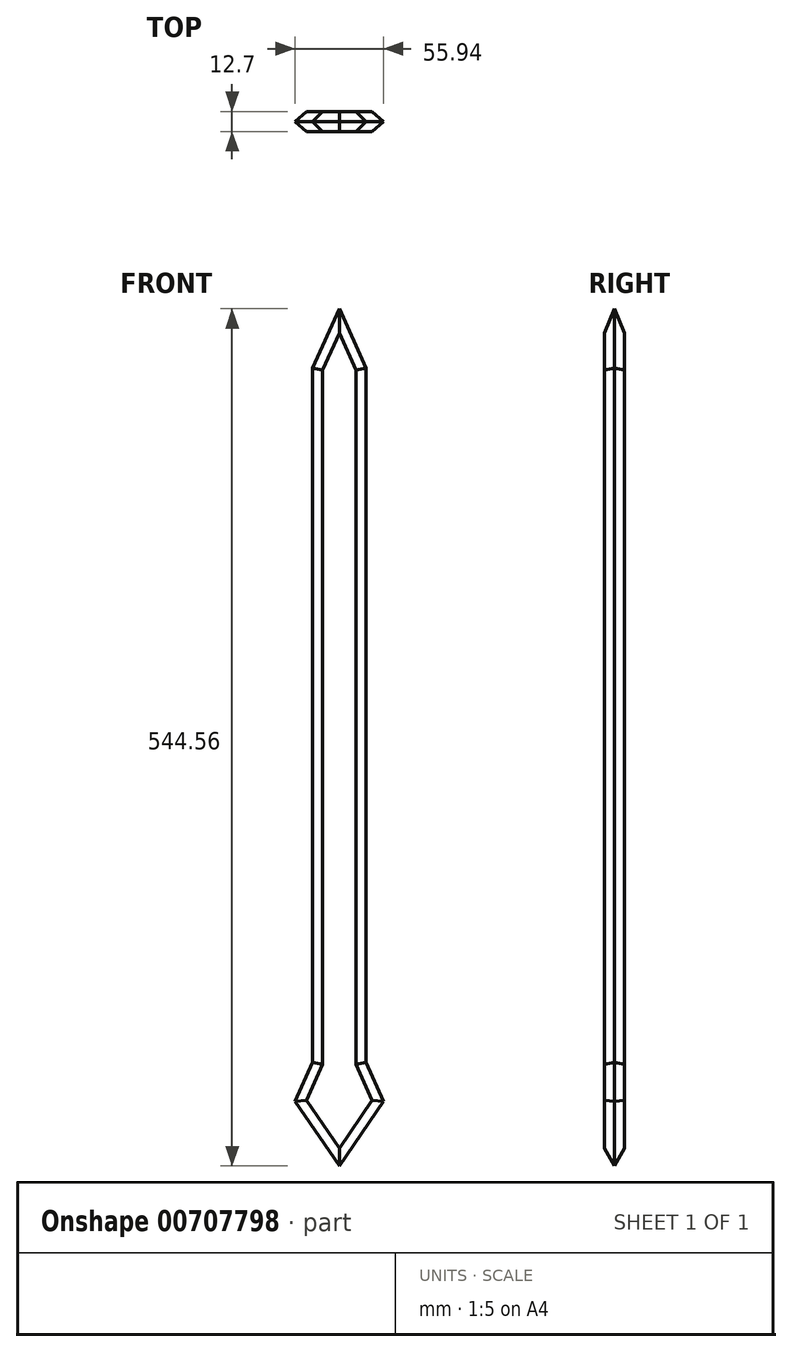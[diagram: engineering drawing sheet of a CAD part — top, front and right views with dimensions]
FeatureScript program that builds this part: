
annotation { "Feature Type Name" : "Feature", "Feature Type Description" : "" }
export const myFeature = defineFeature(function(context is Context, id is Id, definition is map)
    precondition{}
    {
        {
            var Q0;
            Q0=qCreatedBy(makeId("Front.planeOp"),FACE);
            var sketch = newSketch(context, id + "F0", { "sketchPlane" : qUnion([Q0])});
            skLineSegment(sketch, "E0", {"start": v(-27.98, 3.42) * mm, "end": v(0, -37.77) * mm});
            skLineSegment(sketch, "E1", {"start": v(0, -37.77) * mm, "end": v(27.96, 3.42) * mm});
            skLineSegment(sketch, "E2", {"start": v(-27.98, 3.42) * mm, "end": v(-17.14, 28.2) * mm});
            skLineSegment(sketch, "E3", {"start": v(27.96, 3.42) * mm, "end": v(17.08, 28.2) * mm});
            skLineSegment(sketch, "E4", {"start": v(17.08, 28.2) * mm, "end": v(27.96, 3.42) * mm});
            skLineSegment(sketch, "E5", {"start": v(-17.14, 28.2) * mm, "end": v(-17.14, 469.12) * mm});
            skLineSegment(sketch, "E6", {"start": v(-17.14, 469.12) * mm, "end": v(-17.14, 28.2) * mm});
            skLineSegment(sketch, "E7", {"start": v(17.08, 28.2) * mm, "end": v(17.08, 469.12) * mm});
            skLineSegment(sketch, "E8", {"start": v(-17.14, 469.12) * mm, "end": v(0, 506.79) * mm});
            skLineSegment(sketch, "E9", {"start": v(0, 506.79) * mm, "end": v(17.08, 469.12) * mm});
            skSolve(sketch);
        }
        {
            var Q0;
            Q0=makeQuery(id+"F0.imprint","IMPRINT",FACE,{"disambiguationData":[TD([[makeQuery(id+"F0.imprint","IMPRINT",EDGE,{"derivedFrom":sQuery(id+"F0.wireOp",EDGE,"E0")}),1.0]])]});
            extrude(context, id + "F1", {"entities" : qUnion([Q0]), "depth" : 6.35 * mm, "offsetDistance" : 25.4 * mm});
        }
        {
            var Q0;
            Q0=makeQuery(id+"F1.opExtrude","CAP_FACE",FACE,{"disambiguationData":[OSD([sQuery(id+"F0.wireOp",EDGE,"E0"),sQuery(id+"F0.wireOp",EDGE,"E1"),sQuery(id+"F0.wireOp",EDGE,"E2"),sQuery(id+"F0.wireOp",EDGE,"E4"),sQuery(id+"F0.wireOp",EDGE,"E6"),sQuery(id+"F0.wireOp",EDGE,"E7"),sQuery(id+"F0.wireOp",EDGE,"E8"),sQuery(id+"F0.wireOp",EDGE,"E9")])],"isStart":true});
            extrude(context, id + "F2", {"entities" : qUnion([Q0]), "operationType" : NewBodyOperationType.ADD, "depth" : 6.35 * mm, "offsetDistance" : 25.4 * mm});
        }
        {
            var Q0;
            Q0=makeQuery(id+"F1.opExtrude","CAP_FACE",FACE,{"disambiguationData":[OSD([sQuery(id+"F0.wireOp",EDGE,"E0"),sQuery(id+"F0.wireOp",EDGE,"E1"),sQuery(id+"F0.wireOp",EDGE,"E2"),sQuery(id+"F0.wireOp",EDGE,"E4"),sQuery(id+"F0.wireOp",EDGE,"E6"),sQuery(id+"F0.wireOp",EDGE,"E7"),sQuery(id+"F0.wireOp",EDGE,"E8"),sQuery(id+"F0.wireOp",EDGE,"E9")])],"isStart":false});
            var Q1;
            Q1=makeQuery(id+"F2.opExtrude","CAP_FACE",FACE,{"disambiguationData":[OSD([sQuery(id+"F0.wireOp",EDGE,"E0"),sQuery(id+"F0.wireOp",EDGE,"E1"),sQuery(id+"F0.wireOp",EDGE,"E2"),sQuery(id+"F0.wireOp",EDGE,"E4"),sQuery(id+"F0.wireOp",EDGE,"E6"),sQuery(id+"F0.wireOp",EDGE,"E7"),sQuery(id+"F0.wireOp",EDGE,"E8"),sQuery(id+"F0.wireOp",EDGE,"E9")])],"isStart":false});
            chamfer(context, id + "F3", {"entities" : qUnion([Q0, Q1]), "chamferType" : ChamferType.OFFSET_ANGLE, "width" : 6.35 * mm, "oppositeDirection" : false, "angle" : 45 * degree, "tangentPropagation" : true});
        }
    });
